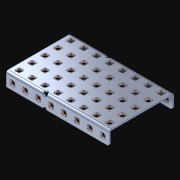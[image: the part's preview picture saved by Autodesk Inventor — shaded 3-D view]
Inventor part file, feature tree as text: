
AUTODESK INVENTOR PART (.ipt)
format: ipt  version: 2021 (Build 250183000, 183)  size: 1,581,568 bytes
history: native  units: in
note: dims shown in document units (in); Inventor stores cm internally (conversion verified against a paired STEP export)
features: extrude x57, other x57, sketch x4, pattern_linear x3
ambient origin geometry x8: Origin, YZ Plane, XZ Plane, XY Plane, X Axis, Y Axis, Z Axis, Center Point
bodies: Solid1 (feature_tree)
feature tree (121):
  pattern_linear  "Rectangular Pattern1"  Spacing1=0.182in  [1 undecoded]
  pattern_linear  "Rectangular Pattern2"  Spacing1=0.046in  [1 undecoded]
  pattern_linear  "Rectangular Pattern3"  Spacing1=0.5in  [1 undecoded]
  extrude  "Extrusion1"  Depth=0.046in
  sketch  "Sketch1"  dims[d0=0.182in]
  other  "Srf1"
  sketch  "Sketch2"  dims[d1=0.046in d2=0.0in]
  other  "Srf2"
  sketch  "Sketch3"  dims[d3=0.182in]
  other  "Srf3"
  other  "Srf4"
  other  "Srf5"
  other  "Srf6"
  other  "Srf7"
  other  "Srf8"
  other  "Srf9"
  other  "Srf10"
  other  "Srf38"
  other  "Srf39"
  other  "Srf40"
  other  "Srf41"
  other  "Srf42"
  other  "Srf43"
  other  "Srf44"
  other  "Srf72"
  other  "Srf73"
  other  "Srf74"
  other  "Srf75"
  other  "Srf76"
  other  "Srf77"
  other  "Srf78"
  other  "Srf79"
  other  "Srf107"
  other  "Srf108"
  other  "Srf109"
  other  "Srf110"
  other  "Srf111"
  other  "Srf112"
  other  "Srf113"
  other  "Srf114"
  other  "Srf142"
  other  "Srf143"
  other  "Srf144"
  other  "Srf145"
  other  "Srf146"
  other  "Srf147"
  other  "Srf148"
  other  "Srf149"
  other  "Srf177"
  other  "Srf178"
  other  "Srf179"
  other  "Srf180"
  other  "Srf181"
  other  "Srf182"
  other  "Srf183"
  other  "Srf184"
  other  "Srf212"
  other  "Srf213"
  other  "Srf214"
  other  "Srf215"
  other  "Srf216"
  other  "Srf217"
  other  "Srf218"
  sketch  "Sketch4"  dims[d4=0.046in d5=0.0in d6=0.182in d7=0.046in d8=0.0in d11=0.5in d12=3.1496in d14=0.5in d15=1.9685in d17=0.5in d18=3.1496in d20=0.5in d21=13.5in d22=0.0in]
  parser-record x1  (decoder bookkeeping rows leaked as tree rows — omitted from the tree; the rows remain in map.json)
  extrude  "ExtrusionSrf1"  Depth=0.046in
  extrude  "ExtrusionSrf2"  Depth=0.046in
  extrude  "ExtrusionSrf3"  Depth=0.046in
  extrude  "ExtrusionSrf4"  Depth=0.046in
  extrude  "ExtrusionSrf5"  Depth=0.046in
  extrude  "ExtrusionSrf6"  TaperAngle=0.0deg  [1 undecoded]
  extrude  "ExtrusionSrf7"  [1 undecoded]
  extrude  "ExtrusionSrf8"  [1 undecoded]
  extrude  "ExtrusionSrf9"  [1 undecoded]
  extrude  "ExtrusionSrf10"  [1 undecoded]
  extrude  "ExtrusionSrf38"  [1 undecoded]
  extrude  "ExtrusionSrf39"  [1 undecoded]
  extrude  "ExtrusionSrf40"  [1 undecoded]
  extrude  "ExtrusionSrf41"  [1 undecoded]
  extrude  "ExtrusionSrf42"  [1 undecoded]
  extrude  "ExtrusionSrf43"  [1 undecoded]
  extrude  "ExtrusionSrf44"  [1 undecoded]
  extrude  "ExtrusionSrf72"  [1 undecoded]
  extrude  "ExtrusionSrf73"  [1 undecoded]
  extrude  "ExtrusionSrf74"  [1 undecoded]
  extrude  "ExtrusionSrf75"  [1 undecoded]
  extrude  "ExtrusionSrf76"  [1 undecoded]
  extrude  "ExtrusionSrf77"  [1 undecoded]
  extrude  "ExtrusionSrf78"  [1 undecoded]
  extrude  "ExtrusionSrf79"  [1 undecoded]
  extrude  "ExtrusionSrf107"  [1 undecoded]
  extrude  "ExtrusionSrf108"  [1 undecoded]
  extrude  "ExtrusionSrf109"  [1 undecoded]
  extrude  "ExtrusionSrf110"  [1 undecoded]
  extrude  "ExtrusionSrf111"  [1 undecoded]
  extrude  "ExtrusionSrf112"  [1 undecoded]
  extrude  "ExtrusionSrf113"  [1 undecoded]
  extrude  "ExtrusionSrf114"  [1 undecoded]
  extrude  "ExtrusionSrf142"  [1 undecoded]
  extrude  "ExtrusionSrf143"  [1 undecoded]
  extrude  "ExtrusionSrf144"  [1 undecoded]
  extrude  "ExtrusionSrf145"  [1 undecoded]
  extrude  "ExtrusionSrf146"  [1 undecoded]
  extrude  "ExtrusionSrf147"  [1 undecoded]
  extrude  "ExtrusionSrf148"  [1 undecoded]
  extrude  "ExtrusionSrf149"  [1 undecoded]
  extrude  "ExtrusionSrf177"  [1 undecoded]
  extrude  "ExtrusionSrf178"  [1 undecoded]
  extrude  "ExtrusionSrf179"  [1 undecoded]
  extrude  "ExtrusionSrf180"  [1 undecoded]
  extrude  "ExtrusionSrf181"  [1 undecoded]
  extrude  "ExtrusionSrf182"  [1 undecoded]
  extrude  "ExtrusionSrf183"  [1 undecoded]
  extrude  "ExtrusionSrf184"  [1 undecoded]
  extrude  "ExtrusionSrf212"  [1 undecoded]
  extrude  "ExtrusionSrf213"  [1 undecoded]
  extrude  "ExtrusionSrf214"  [1 undecoded]
  extrude  "ExtrusionSrf215"  [1 undecoded]
  extrude  "ExtrusionSrf216"  [1 undecoded]
  extrude  "ExtrusionSrf217"  [1 undecoded]
  extrude  "ExtrusionSrf218"  [1 undecoded]
note: 54 required parameter values undecoded (feature->parameter linkage not recoverable at this tier; creation-order binding heuristic only, values carry confidence <= 0.55)
